# Revit family: HVAC_Water-Heaters_Ice-Air_ccHPWH-1
name_source: partatom
category: Mechanical Equipment
units: mm (PartAtom-declared; Revit-internal decimal feet)

## family parameters
Always vertical = Yes
Cut with Voids When Loaded = No
OmniClass Number = 23.65.35.11
OmniClass Title = Supply Water Heaters
Part Type = Normal
Room Calculation Point = No
Round Connector Dimension = Use Diameter
Shared = No
Work Plane-Based = No

## types (6) — shared parameters
Frequency = 60 Hz
Height = 89 "
Manufacturer = Ice Air
Max H/W Temperature = 140°F
Operating Temperature = -13
Phase = 3
Power Factor = 1
Product Material = Ice Air - Metal - Aluminium
Product Page URL = https://www.ice-air.com
URL = https://www.ice-air.com
Voltage = 208 V
Voltage Range = 208-230 V
z_Column Height = 87.03 "
z_Side Panel Height = 32 "
zero-valued in all types: Default Elevation

## per-type parameters (varying)
- ccHPWH275-S: Apparent Load=7190 VA; Condenser Type=Single Wall BPX; Description=ccHPWH Series Cold Climate Heat Pump Water Heater; Full Load Current=104 A; Length=81 "; MCA (with Electric Heat)=134.6; MOCP (with Electric Heat)=175; Pipe Size=2 "; Rated Water Flow=59 GPM; Refrigerant Used=R410A (30.8 Lbs / 15.4 Lbs per circuit); Single Pass Delta-T=10.53; Sound Level (Noise)=≤73; Water Pipe Diameter=2 "; Water Side Pressure Loss=118.9; Weight=1555.00 lbf; Width=39 "; z_Fan Blade Diameter=29 "; z_Fan Distance=5 "; z_Fan Grill=Family2 : s; z_Fan Guard Diameter=31 "; z_Fan Guard WD=35 "; z_Pipe Size=2 "; z_Second Ref Side Panel Height=0 "; z_Side Column Width=3.5 "; z_ccHPWH275_Visibility=Yes; z_ccHPWH550_Visibility=No
- ccHPWH275-D: Apparent Load=7377 VA; Condenser Type=Double Wall BPX; Description=ccHPWH Series Cold Climate Heat Pump Water Heater; Full Load Current=106 A; Length=81 "; MCA (with Electric Heat)=134.6; MOCP (with Electric Heat)=175; Pipe Size=2 "; Rated Water Flow=59 GPM; Refrigerant Used=R410A (30.8 Lbs / 15.4 Lbs per circuit); Single Pass Delta-T=10.37; Sound Level (Noise)=≤73; Water Pipe Diameter=2 "; Water Side Pressure Loss=11.7; Weight=1555.00 lbf; Width=39 "; z_Fan Blade Diameter=29 "; z_Fan Distance=5 "; z_Fan Grill=Family2 : s; z_Fan Guard Diameter=31 "; z_Fan Guard WD=35 "; z_Pipe Size=2 "; z_Second Ref Side Panel Height=0 "; z_Side Column Width=3.5 "; z_ccHPWH275_Visibility=Yes; z_ccHPWH550_Visibility=No
- ccHPWH275-SC: Apparent Load=7190 VA; Description=ccHPWH-SC Series Cold Climate Heat Pump Water Chiller/Heater; Full Load Current=104 A; Heat Exchanger Type=Single Wall Brazed Plate HXR; Length=81 "; MCA (with Electric Heat)=134.6; MOCP (with Electric Heat)=175; Pipe Size=2 "; Rated Water Flow=73 GPM; Refrigerant Used=R410A (30.8 Lbs / 15.4 Lbs per circuit); Sound Level (Noise)=≤71; Water Pipe Diameter=2 "; Water Side Pressure Loss=11.7; Weight=1500.00 lbf; Width=39 "; z_Fan Blade Diameter=29 "; z_Fan Distance=5 "; z_Fan Grill=Family2 : s; z_Fan Guard Diameter=31 "; z_Fan Guard WD=35 "; z_Pipe Size=2 "; z_Second Ref Side Panel Height=0 "; z_Side Column Width=3.5 "; z_ccHPWH275_Visibility=Yes; z_ccHPWH550_Visibility=No
- ccHPWH550-S: Apparent Load=14172 VA; Condenser Type=Single Wall BPX; Description=ccHPWH Series Cold Climate Heat Pump Water Heater; Full Load Current=204 A; Length=95 "; MCA (with Electric Heat)=254.4; MOCP (with Electric Heat)=300; Pipe Size=3 "; Rated Water Flow=119 GPM; Refrigerant Used=R410A (61.7 Lbs / 15.4 Lbs per circuit); Single Pass Delta-T=11.00; Sound Level (Noise)=≤75; Water Pipe Diameter=3 "; Water Side Pressure Loss=10.80; Weight=2950.00 lbf; Width=51 "; z_Fan Blade Diameter=36.5 "; z_Fan Distance=2 "; z_Fan Grill=Family2 : l; z_Fan Guard Diameter=38.5 "; z_Fan Guard WD=42.5 "; z_Pipe Size=3 "; z_Second Ref Side Panel Height=3.58 "; z_Side Column Width=7.87 "; z_ccHPWH275_Visibility=No; z_ccHPWH550_Visibility=Yes
- ccHPWH550-D: Apparent Load=14754 VA; Condenser Type=Double Wall BPX; Description=ccHPWH Series Cold Climate Heat Pump Water Heater; Full Load Current=213 A; Length=95 "; MCA (with Electric Heat)=254.4; MOCP (with Electric Heat)=300; Pipe Size=3 "; Rated Water Flow=119 GPM; Refrigerant Used=R410A (61.7 Lbs / 15.4 Lbs per circuit); Single Pass Delta-T=10.80; Sound Level (Noise)=≤75; Water Pipe Diameter=3 "; Water Side Pressure Loss=16.51; Weight=2950.00 lbf; Width=51 "; z_Fan Blade Diameter=36.5 "; z_Fan Distance=2 "; z_Fan Grill=Family2 : l; z_Fan Guard Diameter=38.5 "; z_Fan Guard WD=42.5 "; z_Pipe Size=3 "; z_Second Ref Side Panel Height=3.58 "; z_Side Column Width=7.87 "; z_ccHPWH275_Visibility=No; z_ccHPWH550_Visibility=Yes
- ccHPWH550-SC: Apparent Load=14172 VA; Description=ccHPWH-SC Series Cold Climate Heat Pump Water Chiller/Heater; Full Load Current=204 A; Heat Exchanger Type=Single Wall Brazed Plate HXR; Length=95 "; MCA (with Electric Heat)=254.4; MOCP (with Electric Heat)=300; Pipe Size=3 "; Rated Water Flow=130 GPM; Refrigerant Used=R410A (61.7 Lbs / 15.4 Lbs per circuit); Sound Level (Noise)=≤76; Water Pipe Diameter=3 "; Water Side Pressure Loss=16.51; Weight=2850.00 lbf; Width=51 "; z_Fan Blade Diameter=36.5 "; z_Fan Distance=2 "; z_Fan Grill=Family2 : l; z_Fan Guard Diameter=38.5 "; z_Fan Guard WD=42.5 "; z_Pipe Size=3 "; z_Second Ref Side Panel Height=3.58 "; z_Side Column Width=7.87 "; z_ccHPWH275_Visibility=No; z_ccHPWH550_Visibility=Yes

note: column(s) folded — value = type name in every type: Model

## geometry (parser evidence)
native form markers: Sweep x10
no freeform markers — native parametric forms only
